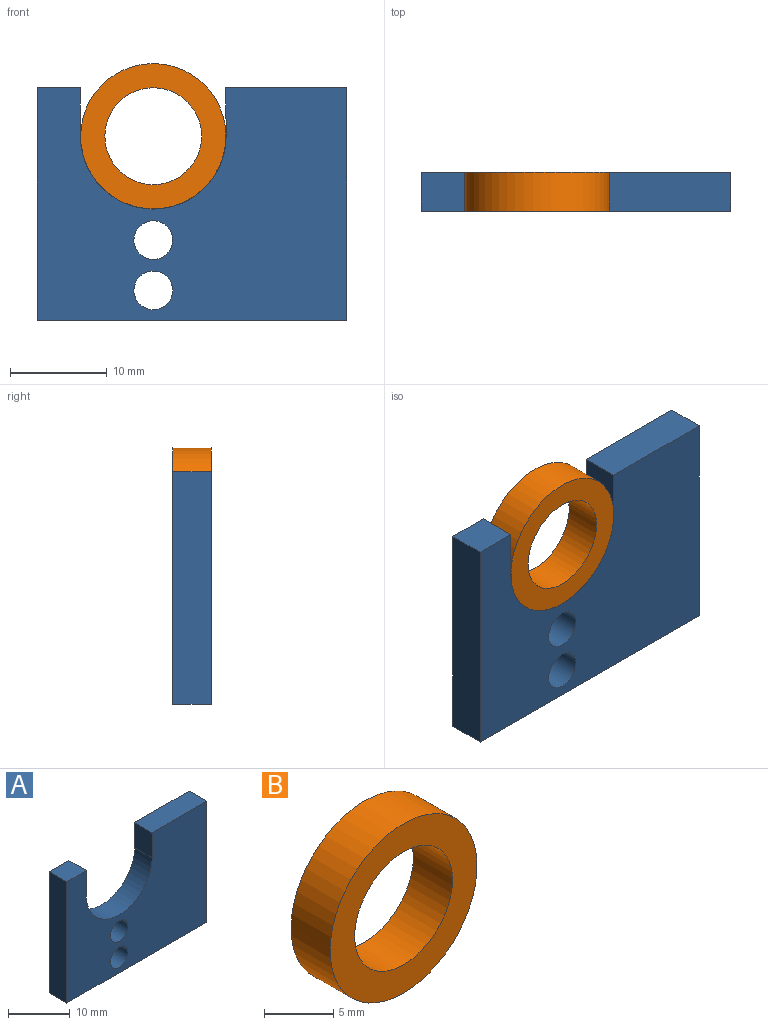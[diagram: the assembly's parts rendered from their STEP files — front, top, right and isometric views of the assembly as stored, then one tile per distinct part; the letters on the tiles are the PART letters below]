
ASSEMBLY  parts=2 mates=1
PART A: 12 faces, bbox 32x4x24 mm
  f0: plane 24x4mm, normal (-1,0,0), area 96mm2, adj f1,f8,f10,f11
  f1: plane 32x4mm, normal (0,0,-1), area 128mm2, adj f0,f2,f10,f11
  f2: plane 24x4mm, normal (1,0,0), area 96mm2, adj f1,f3,f10,f11
  f3: plane 12.51x4mm, normal (0,0,1), area 50mm2, adj f2,f4,f10,f11
  f4: plane 5x4mm, normal (-1,0,-0.01), area 20mm2, adj f3,f5,f10,f11
  f5: cylinder r=7.52mm len=15.05mm, axis (0,1,0), area 94.6mm2, adj f4,f6,f10,f11
  f6: plane 5x4mm, normal (1,0,0), area 20mm2, adj f5,f8,f10,f11
  f7: cylinder r=2mm len=4mm, axis (0,1,0), area 50.3mm2, adj f10,f11
  f8: plane 4.48x4mm, normal (0,0,1), area 17.9mm2, adj f0,f6,f10,f11
  f9: cylinder r=2mm len=4mm, axis (0,1,0), area 50.3mm2, adj f10,f11
  f10: plane 32x24mm, normal (0,-1,0), area 578.8mm2, adj f0,f1,f2,f3,f4,f5,f6,f7
  f11: plane 32x24mm, normal (0,1,0), area 578.8mm2, adj f0,f1,f2,f3,f4,f5,f6,f7
PART B: 4 faces, bbox 15x4x15 mm
  f0: cylinder r=5mm len=10mm, axis (0,1,0), area 125.7mm2, adj f2,f3
  f1: cylinder r=7.5mm len=15mm, axis (0,1,0), area 188.5mm2, adj f2,f3
  f2: plane 15x15mm, normal (0,-1,0), area 98.2mm2, adj f0,f1
  f3: plane 15x15mm, normal (0,1,0), area 98.2mm2, adj f0,f1
PLACE A t=(-0.66,1.37,-0.51)mm fixed
PLACE B t=(-0.66,-0.63,18.49)mm
MATE pin_slot A.f5 <-> B.f1  axis (0,-1,0) through (-0.66,-2.63,18.49)mm
